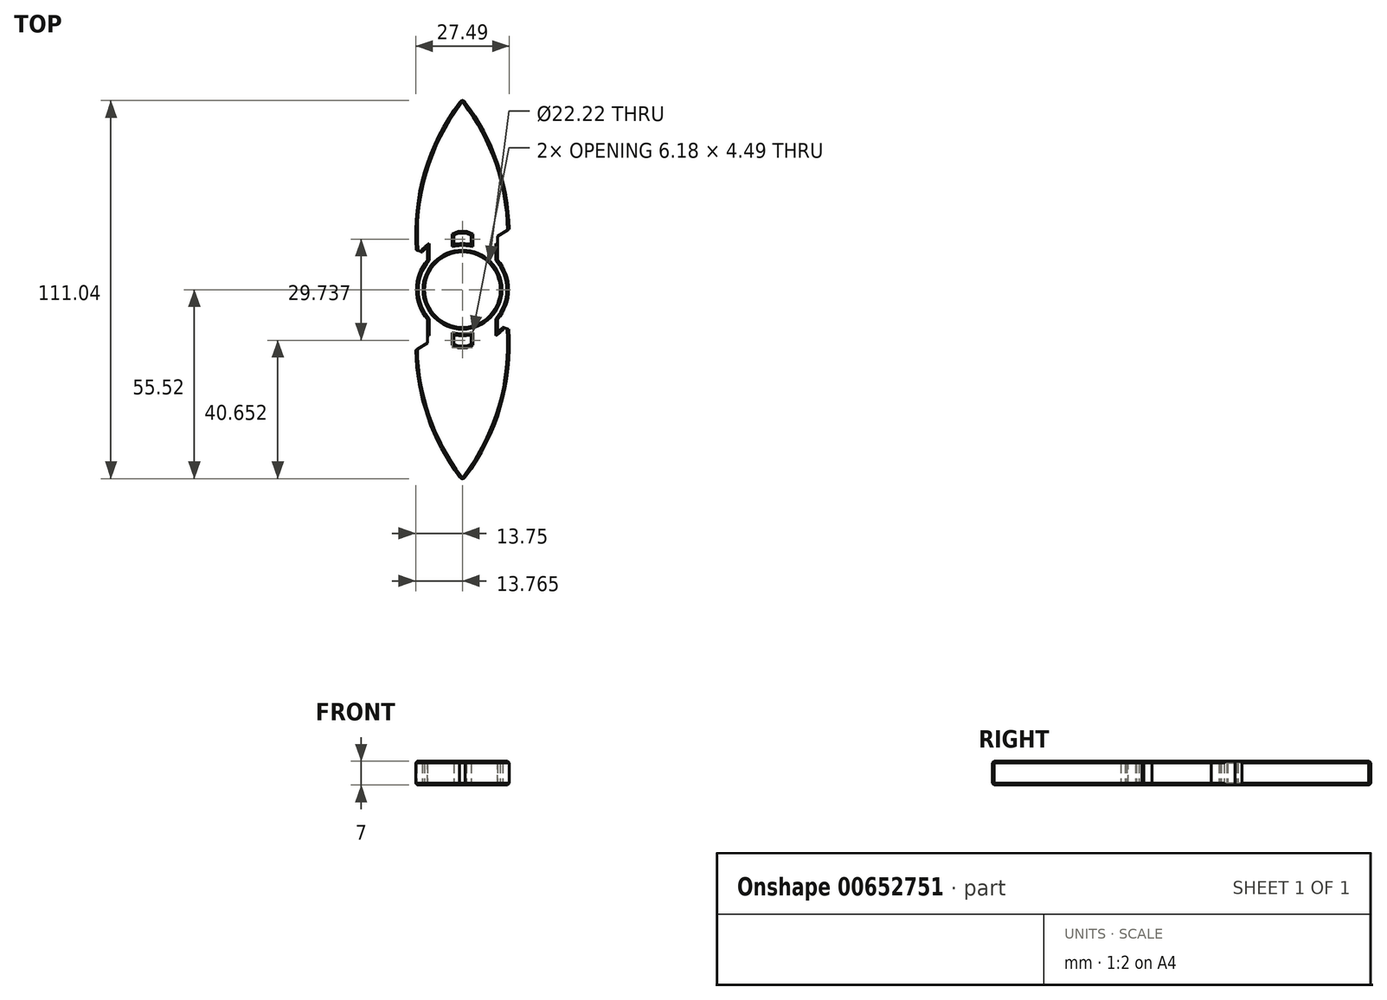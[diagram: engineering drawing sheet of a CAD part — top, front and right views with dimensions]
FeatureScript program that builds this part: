
annotation { "Feature Type Name" : "Feature", "Feature Type Description" : "" }
export const myFeature = defineFeature(function(context is Context, id is Id, definition is map)
    precondition{}
    {
        {
            var Q0;
            Q0=qCreatedBy(makeId("Top.planeOp"),FACE);
            var sketch = newSketch(context, id + "F0", { "sketchPlane" : qUnion([Q0])});
            skCircle(sketch, "E0", {"center": v(0, 0) * mm, "radius": 11 * mm});
            skCircle(sketch, "E1.0", {"center": v(0, 0) * mm, "radius": 4 * mm});
            skCircle(sketch, "E2.0", {"center": v(0, 0) * mm, "radius": 11.1 * mm});
            skCircle(sketch, "E3.0", {"center": v(0, 0) * mm, "radius": 13.5 * mm});
            skLineSegment(sketch, "E4.MirrorCS", {"start": v(-2.57, -16.02) * mm, "end": v(-1.13, -16.61) * mm});
            skLineSegment(sketch, "E5.MirrorCS", {"start": v(2.6, -16) * mm, "end": v(1.16, -16.58) * mm});
            skArc(sketch, "E6.MirrorCS", {"start": v(10.3, -12.5) * mm, "mid": v(11.94, -10.95) * mm, "end": v(13.35, -9.17) * mm});
            skArc(sketch, "E7.MirrorCS", {"start": v(-10.3, -12.5) * mm, "mid": v(-11.95, -10.95) * mm, "end": v(-13.36, -9.17) * mm});
            skLineSegment(sketch, "E8.MirrorCS", {"start": v(10.3, -12.5) * mm, "end": v(10.3, -8.73) * mm});
            skArc(sketch, "E9.MirrorCS", {"start": v(0.8, -55) * mm, "mid": v(11.46, -33.28) * mm, "end": v(13.35, -9.17) * mm});
            skArc(sketch, "E10.MirrorCS", {"start": v(-0.82, -55) * mm, "mid": v(-11.47, -33.28) * mm, "end": v(-13.36, -9.17) * mm});
            skArc(sketch, "E11", {"start": v(-0.82, -55) * mm, "mid": v(0, -55.52) * mm, "end": v(0.8, -55) * mm});
            skLineSegment(sketch, "E12", {"start": v(-2.57, -16.02) * mm, "end": v(-2.57, -13.25) * mm});
            skLineSegment(sketch, "E13", {"start": v(2.6, -16) * mm, "end": v(2.6, -13.25) * mm});
            skLineSegment(sketch, "E14", {"start": v(-10.3, -12.5) * mm, "end": v(-10.3, -8.72) * mm});
            skArc(sketch, "E15.MirrorCS", {"start": v(-0.82, 55) * mm, "mid": v(-11.47, 33.28) * mm, "end": v(-13.36, 9.17) * mm});
            skArc(sketch, "E16.MirrorCS", {"start": v(-0.82, 55) * mm, "mid": v(0, 55.52) * mm, "end": v(0.8, 55) * mm});
            skArc(sketch, "E17.MirrorCS", {"start": v(0.8, 55) * mm, "mid": v(11.46, 33.28) * mm, "end": v(13.35, 9.17) * mm});
            skArc(sketch, "E18.MirrorCS", {"start": v(10.3, 12.5) * mm, "mid": v(11.94, 10.95) * mm, "end": v(13.35, 9.17) * mm});
            skLineSegment(sketch, "E19.MirrorCS", {"start": v(10.3, 12.5) * mm, "end": v(10.3, 8.73) * mm});
            skLineSegment(sketch, "E20.MirrorCS", {"start": v(2.6, 16) * mm, "end": v(2.6, 13.25) * mm});
            skLineSegment(sketch, "E21.MirrorCS", {"start": v(2.6, 16) * mm, "end": v(1.16, 16.58) * mm});
            skLineSegment(sketch, "E22.MirrorCS", {"start": v(-2.57, 16.02) * mm, "end": v(-1.13, 16.61) * mm});
            skLineSegment(sketch, "E23.MirrorCS", {"start": v(-2.57, 16.02) * mm, "end": v(-2.57, 13.25) * mm});
            skLineSegment(sketch, "E24.MirrorCS", {"start": v(-10.3, 12.5) * mm, "end": v(-10.3, 8.72) * mm});
            skArc(sketch, "E25.MirrorCS", {"start": v(-10.3, 12.5) * mm, "mid": v(-11.95, 10.95) * mm, "end": v(-13.36, 9.17) * mm});
            skLineSegment(sketch, "E26", {"start": v(-1.13, 16.61) * mm, "end": v(1.16, 16.58) * mm});
            skLineSegment(sketch, "E27", {"start": v(-1.13, -16.61) * mm, "end": v(1.16, -16.58) * mm});
            skSolve(sketch);
        }
        {
            var Q0;
            Q0=makeQuery(id+"F0.imprint","IMPRINT",FACE,{"disambiguationData":[TD([[makeQuery(id+"F0.imprint","IMPRINT",EDGE,{"derivedFrom":sQuery(id+"F0.wireOp",EDGE,"wvD0B3R9-YAtX-Gxpq-sWCv-gH5YwA1o8Xyg")}),1.0]])]});
            var Q1;
            Q1=makeQuery(id+"F0.imprint","IMPRINT",FACE,{"disambiguationData":[TD([[makeQuery(id+"F0.imprint","IMPRINT",EDGE,{"derivedFrom":sQuery(id+"F0.wireOp",EDGE,"E2.0")}),-1.0]])]});
            var Q2;
            Q2=makeQuery(id+"F0.imprint","IMPRINT",FACE,{"disambiguationData":[TD([[makeQuery(id+"F0.imprint","IMPRINT",EDGE,{"derivedFrom":sQuery(id+"F0.wireOp",EDGE,"2fd621de-1b4b-4d62-af44-6a63c9a9710d.1.0")}),-1.0]])]});
            var Q3;
            {var subQ0=sQuery(id+"F0.wireOp",EDGE,"af42e5d3-754a-4d1d-a53d-a0419badffb7.1.0");Q3=makeQuery(id+"F0.imprint","IMPRINT",FACE,{"disambiguationData":[TD([[makeQuery(id+"F0.imprint","IMPRINT",EDGE,{"derivedFrom":subQ0}),1.0]])]});}
            var Q4;
            {var subQ1=sQuery(id+"F0.wireOp",EDGE,"2zH8kRDW-wvDr-pyvj-1Biy-DdkABgr5Na4A");Q4=makeQuery(id+"F0.imprint","IMPRINT",FACE,{"disambiguationData":[TD([[makeQuery(id+"F0.imprint","IMPRINT",EDGE,{"derivedFrom":subQ1}),1.0]])]});}
            var Q5;
            {var subQ2=sQuery(id+"F0.wireOp",EDGE,"99f32757-464d-478a-b034-0b54129395020.MirrorCS");Q5=makeQuery(id+"F0.imprint","IMPRINT",FACE,{"disambiguationData":[TD([[makeQuery(id+"F0.imprint","IMPRINT",EDGE,{"derivedFrom":subQ2}),-1.0]])]});}
            var Q6;
            {var subQ0=sQuery(id+"F0.wireOp",EDGE,"nOQlTlEd-rPO4-0JiK-N7wF-rGotaaLiI0Ob");Q6=makeQuery(id+"F0.imprint","IMPRINT",FACE,{"disambiguationData":[TD([[makeQuery(id+"F0.imprint","IMPRINT",EDGE,{"derivedFrom":subQ0}),-1.0]])]});}
            var Q7;
            {var subQ1=sQuery(id+"F0.wireOp",EDGE,"E5.MirrorCS");Q7=makeQuery(id+"F0.imprint","IMPRINT",FACE,{"disambiguationData":[TD([[makeQuery(id+"F0.imprint","IMPRINT",EDGE,{"derivedFrom":subQ1}),1.0]])]});}
            var Q8;
            {var subQ2=sQuery(id+"F0.wireOp",EDGE,"E4.MirrorCS");Q8=makeQuery(id+"F0.imprint","IMPRINT",FACE,{"disambiguationData":[TD([[makeQuery(id+"F0.imprint","IMPRINT",EDGE,{"derivedFrom":subQ2}),-1.0]])]});}
            var Q9;
            {var subQ0=sQuery(id+"F0.wireOp",EDGE,"c4c8e9f6-6721-4071-ad00-793d0db8e68d0.MirrorCS");Q9=makeQuery(id+"F0.imprint","IMPRINT",FACE,{"disambiguationData":[TD([[makeQuery(id+"F0.imprint","IMPRINT",EDGE,{"derivedFrom":subQ0}),1.0]])]});}
            var Q10;
            Q10=makeQuery(id+"F0.imprint","IMPRINT",FACE,{"disambiguationData":[TD([[makeQuery(id+"F0.imprint","IMPRINT",EDGE,{"derivedFrom":sQuery(id+"F0.wireOp",EDGE,"E15.MirrorCS")}),1.0]])]});
            extrude(context, id + "F1", {"entities" : qUnion([Q0, Q1, Q2, Q3, Q4, Q5, Q6, Q7, Q8, Q9, Q10]), "depth" : 7 * mm, "offsetDistance" : 25 * mm});
        }
        {
            var Q0;
            Q0=makeQuery(id+"F1.opExtrude","CAP_FACE",FACE,{"disambiguationData":[OSD([sQuery(id+"F0.wireOp",EDGE,"E2.0"),sQuery(id+"F0.wireOp",EDGE,"E3.0"),sQuery(id+"F0.wireOp",EDGE,"wvD0B3R9-YAtX-Gxpq-sWCv-gH5YwA1o8Xyg"),sQuery(id+"F0.wireOp",EDGE,"Yzvk527z-9KrF-P72y-4Wso-r2fertBEkhr8"),sQuery(id+"F0.wireOp",EDGE,"4bf20e14-99d5-461b-afae-550b82235c6d.0"),sQuery(id+"F0.wireOp",EDGE,"2zH8kRDW-wvDr-pyvj-1Biy-DdkABgr5Na4A"),sQuery(id+"F0.wireOp",EDGE,"bk0HmgWE-uhqc-ZVK6-LUaC-9pWmphtK6rCV"),sQuery(id+"F0.wireOp",EDGE,"0d688302-5a5e-4cb5-b386-0c9360da8733.trimOffspring"),sQuery(id+"F0.wireOp",EDGE,"2fd621de-1b4b-4d62-af44-6a63c9a9710d.1.0"),sQuery(id+"F0.wireOp",EDGE,"2fd621de-1b4b-4d62-af44-6a63c9a9710d.1.1"),sQuery(id+"F0.wireOp",EDGE,"2fd621de-1b4b-4d62-af44-6a63c9a9710d.1.2"),sQuery(id+"F0.wireOp",EDGE,"2fd621de-1b4b-4d62-af44-6a63c9a9710d.1.3"),sQuery(id+"F0.wireOp",EDGE,"2fd621de-1b4b-4d62-af44-6a63c9a9710d.1.4"),sQuery(id+"F0.wireOp",EDGE,"2fd621de-1b4b-4d62-af44-6a63c9a9710d.1.5")])],"isStart":false});
            var Q1;
            Q1=makeQuery(id+"F1.opExtrude","CAP_FACE",FACE,{"disambiguationData":[OSD([sQuery(id+"F0.wireOp",EDGE,"E2.0"),sQuery(id+"F0.wireOp",EDGE,"E3.0"),sQuery(id+"F0.wireOp",EDGE,"wvD0B3R9-YAtX-Gxpq-sWCv-gH5YwA1o8Xyg"),sQuery(id+"F0.wireOp",EDGE,"Yzvk527z-9KrF-P72y-4Wso-r2fertBEkhr8"),sQuery(id+"F0.wireOp",EDGE,"4bf20e14-99d5-461b-afae-550b82235c6d.0"),sQuery(id+"F0.wireOp",EDGE,"2zH8kRDW-wvDr-pyvj-1Biy-DdkABgr5Na4A"),sQuery(id+"F0.wireOp",EDGE,"bk0HmgWE-uhqc-ZVK6-LUaC-9pWmphtK6rCV"),sQuery(id+"F0.wireOp",EDGE,"0d688302-5a5e-4cb5-b386-0c9360da8733.trimOffspring"),sQuery(id+"F0.wireOp",EDGE,"2fd621de-1b4b-4d62-af44-6a63c9a9710d.1.0"),sQuery(id+"F0.wireOp",EDGE,"2fd621de-1b4b-4d62-af44-6a63c9a9710d.1.1"),sQuery(id+"F0.wireOp",EDGE,"2fd621de-1b4b-4d62-af44-6a63c9a9710d.1.2"),sQuery(id+"F0.wireOp",EDGE,"2fd621de-1b4b-4d62-af44-6a63c9a9710d.1.3"),sQuery(id+"F0.wireOp",EDGE,"2fd621de-1b4b-4d62-af44-6a63c9a9710d.1.4"),sQuery(id+"F0.wireOp",EDGE,"2fd621de-1b4b-4d62-af44-6a63c9a9710d.1.5")])],"isStart":true});
            chamfer(context, id + "F2", {"entities" : qUnion([Q0, Q1]), "width" : .5 * mm, "tangentPropagation" : true});
        }
        {
            var Q0;
            Q0=makeQuery(id+"F1.opExtrude","SWEPT_EDGE",EDGE,{"disambiguationData":[OSD([sQuery(id+"F0.wireOp",EDGE,"E7.MirrorCS"),sQuery(id+"F0.wireOp",EDGE,"E10.MirrorCS")])]});
            var Q1;
            Q1=makeQuery(id+"F1.opExtrude","SWEPT_EDGE",EDGE,{"disambiguationData":[OSD([sQuery(id+"F0.wireOp",EDGE,"E17.MirrorCS"),sQuery(id+"F0.wireOp",EDGE,"E18.MirrorCS")])]});
            chamfer(context, id + "F3", {"entities" : qUnion([Q0, Q1]), "width" : 4 * mm, "tangentPropagation" : true});
        }
        {
            var Q0;
            Q0=makeQuery(id+"F1.opExtrude","SWEPT_EDGE",EDGE,{"disambiguationData":[OSD([sQuery(id+"F0.wireOp",EDGE,"E15.MirrorCS"),sQuery(id+"F0.wireOp",EDGE,"E25.MirrorCS")])]});
            var Q1;
            Q1=makeQuery(id+"F1.opExtrude","SWEPT_EDGE",EDGE,{"disambiguationData":[OSD([sQuery(id+"F0.wireOp",EDGE,"E6.MirrorCS"),sQuery(id+"F0.wireOp",EDGE,"E9.MirrorCS")])]});
            chamfer(context, id + "F4", {"entities" : qUnion([Q0, Q1]), "width" : 1 * mm, "tangentPropagation" : true});
        }
    });
